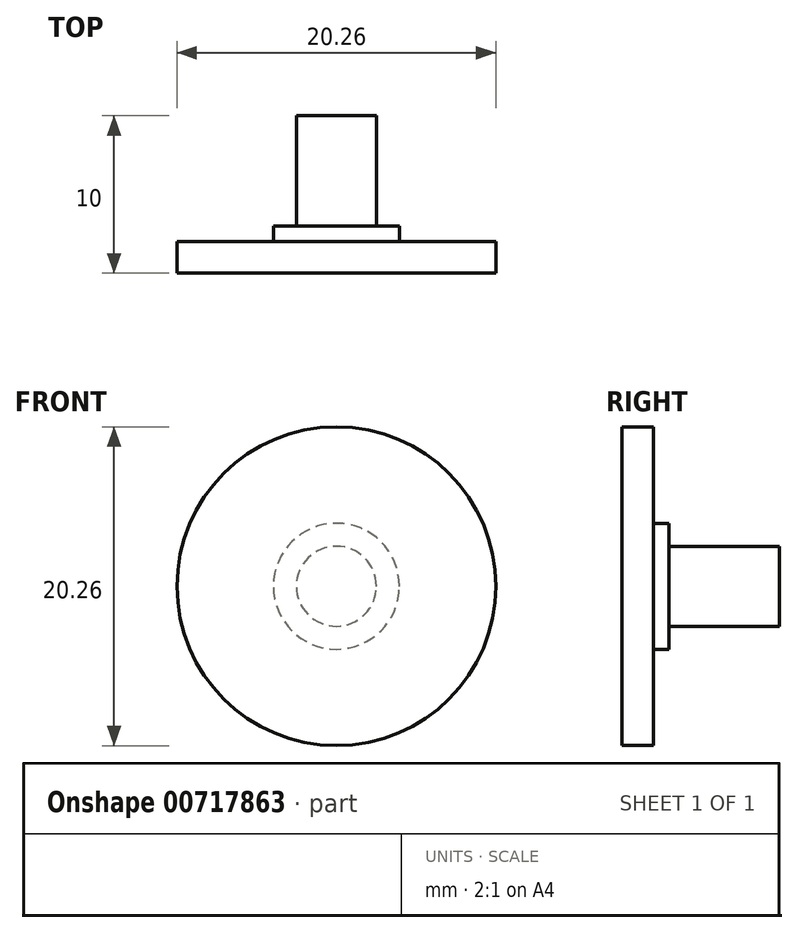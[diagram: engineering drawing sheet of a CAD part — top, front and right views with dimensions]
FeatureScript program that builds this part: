
annotation { "Feature Type Name" : "Feature", "Feature Type Description" : "" }
export const myFeature = defineFeature(function(context is Context, id is Id, definition is map)
    precondition{}
    {
        {
            var Q0;
            Q0=qCreatedBy(makeId("Front.planeOp"),FACE);
            var sketch = newSketch(context, id + "F0", { "sketchPlane" : qUnion([Q0])});
            skCircle(sketch, "E0", {"center": v(0, 0) * mm, "radius": 10.12 * mm});
            skSolve(sketch);
        }
        {
            var Q0;
            Q0=makeQuery(id+"F0.imprint","IMPRINT",FACE,{"disambiguationData":[TD([[makeQuery(id+"F0.imprint","IMPRINT",EDGE,{"derivedFrom":sQuery(id+"F0.wireOp",EDGE,"E0")}),1.0]])]});
            extrude(context, id + "F1", {"entities" : qUnion([Q0]), "depth" : 2 * mm, "offsetDistance" : 25 * mm});
        }
        {
            var Q0;
            Q0=makeQuery(id+"F1.opExtrude","CAP_FACE",FACE,{"disambiguationData":[OSD([sQuery(id+"F0.wireOp",EDGE,"E0")])],"isStart":true});
            var sketch = newSketch(context, id + "F2", { "sketchPlane" : qUnion([Q0])});
            skCircle(sketch, "E1", {"center": v(0, 0) * mm, "radius": 4 * mm});
            skSolve(sketch);
        }
        {
            var Q0;
            Q0=makeQuery(id+"F2.imprint","IMPRINT",FACE,{"disambiguationData":[TD([[makeQuery(id+"F2.imprint","IMPRINT",EDGE,{"derivedFrom":sQuery(id+"F2.wireOp",EDGE,"E1")}),1.0]])]});
            extrude(context, id + "F3", {"entities" : qUnion([Q0]), "operationType" : NewBodyOperationType.ADD, "depth" : 1 * mm, "offsetDistance" : 25 * mm});
        }
        {
            var Q0;
            Q0=makeQuery(id+"F3.opExtrude","CAP_FACE",FACE,{"disambiguationData":[OSD([sQuery(id+"F2.wireOp",EDGE,"E1")])],"isStart":false});
            var sketch = newSketch(context, id + "F4", { "sketchPlane" : qUnion([Q0])});
            skCircle(sketch, "E2", {"center": v(0, 0) * mm, "radius": 2.54 * mm});
            skSolve(sketch);
        }
        {
            var Q0;
            Q0=makeQuery(id+"F4.imprint","IMPRINT",FACE,{"disambiguationData":[TD([[makeQuery(id+"F4.imprint","IMPRINT",EDGE,{"derivedFrom":sQuery(id+"F4.wireOp",EDGE,"E2")}),1.0]])]});
            extrude(context, id + "F5", {"entities" : qUnion([Q0]), "operationType" : NewBodyOperationType.ADD, "depth" : 7 * mm, "offsetDistance" : 25 * mm});
        }
    });
